# Revit family: Keor COMPACT Cabinets
name_source: partatom
category: Modèles génériques
revit_build: Autodesk Revit 2018 (Build: 20170223_1515(x64)
units: mm (PartAtom-declared; Revit-internal decimal feet)

## family parameters
Basée sur le plan de construction = Non
Cote de connecteur circulaire = Utiliser le diamètre
Couper avec des vides une fois chargée = Non
Numéro OmniClass = 23.80.10.24.17
Partagée = Non
Peut héberger une armature = Non
Point de calcul de pièce = Non
Titre OmniClass = Uninterrupted Power Supply (UPS) Units
Toujours verticalement = Oui
Type d'élément = Normal

## types (4) — shared parameters
Acoustic Noise at 1m (dBA) = < 52
Architecture = Stand Alone or Distributed Parallel up to 6 units
Audible alarm = Acoustic alarms and warnings
BackFeed protection = Embedded
Battery type = VRLA – AGM Maintenance free
By-pass = Builtin  Automatic and Mainteinance Bypass
Color = RAL9017 (Black-cabinet) RAL9003 (White-control panel)
Communication ports = RS232, Genset, Progammable 4 Relays contacts
Compatibility with Diesel Generators = Oui
Control Panel Display = Colour Touch screen 4.3
Crest Factor = 3:1
Dimensions (W x D x H) mm = 260 x 850 x 890
Dual Input = Oui
Efficiency = up to 96% *
Efficiency in ECO mode = up to 98,5%
Emergency Power Off (EPO) = Oui
Fabricant = Legrand
General Conditions of Use = https://export.legrand.com
Input Frequency = 40-70 Hz
Input Voltage = 400V (3Ph+N+PE)
Input Voltage Range (Ph-Ph) = ±20% @100% load,  -40/+20% @50% load
Input power factor = >0.99
Modèle = Keor Compact
Net interface slot = Yes for optional net Interface card (SNMP)
Operating Temperature (°C) = 0 - 40 ᵒC (Recommended temperature for longer Battery Life:  20-25ᵒC)
Output Voltage (VAC) = 380/400/415V
Output frequency (nominale) = 50 /60 Hz (Adjustable from front panel)
Output frequency tolerance = ±1Hz/±3Hz adjustable synch with Mains;  ±0,01% Free Run
Output power factor = 0.9
Output voltage tolerance = ± 1%
Overload Capability = 60 min at 110%, 10 min at 125%; 1 min at 150%
Protection degree = IP20
Reference product standards = IEC/EN 62040-1, IEC/EN 62040-2, IEC/EN 62040-3
Relative Humidity Range = 20-95% (Non-Condensing)
Remote Management = Availble
THD of input current = < 3% at full load
THD of output voltage = < 2% with linear load,  <5% with distorted load
Technology = On-line double conversion VFI-SS-111
Ventilation = Forced with FANs from front to rear
Waveform = Sinusoidal

## per-type parameters (varying)
| type | Active Power (kVA) | Internal batteries | Max Heat Disipation at nominal load W battery in recharge | Nominal Power (kVA) | Quantity of batteries | Weight (without Batteries) kg |
| 311094 Keor Compact Battery Empty |  | Non |  |  | Empty up to 80blocks 9Ah | 74 |
| 311095 Keor Compact Battery Cabinet 10kVA | 9 | Oui | 600W | 10 | 2x30x9Ah | 0 |
| 311096 Keor Compact Battery Cabinet 15kVA | 13.5 | Non | 900W | 15 | 2x36x9Ah | 0 |
| 311097 Keor Compact Battery Cabinet 20kVA | 18 | Oui | 1300W | 20 | 2x40x9Ah | 0 |

note: column(s) folded — value = type name in every type: Description
